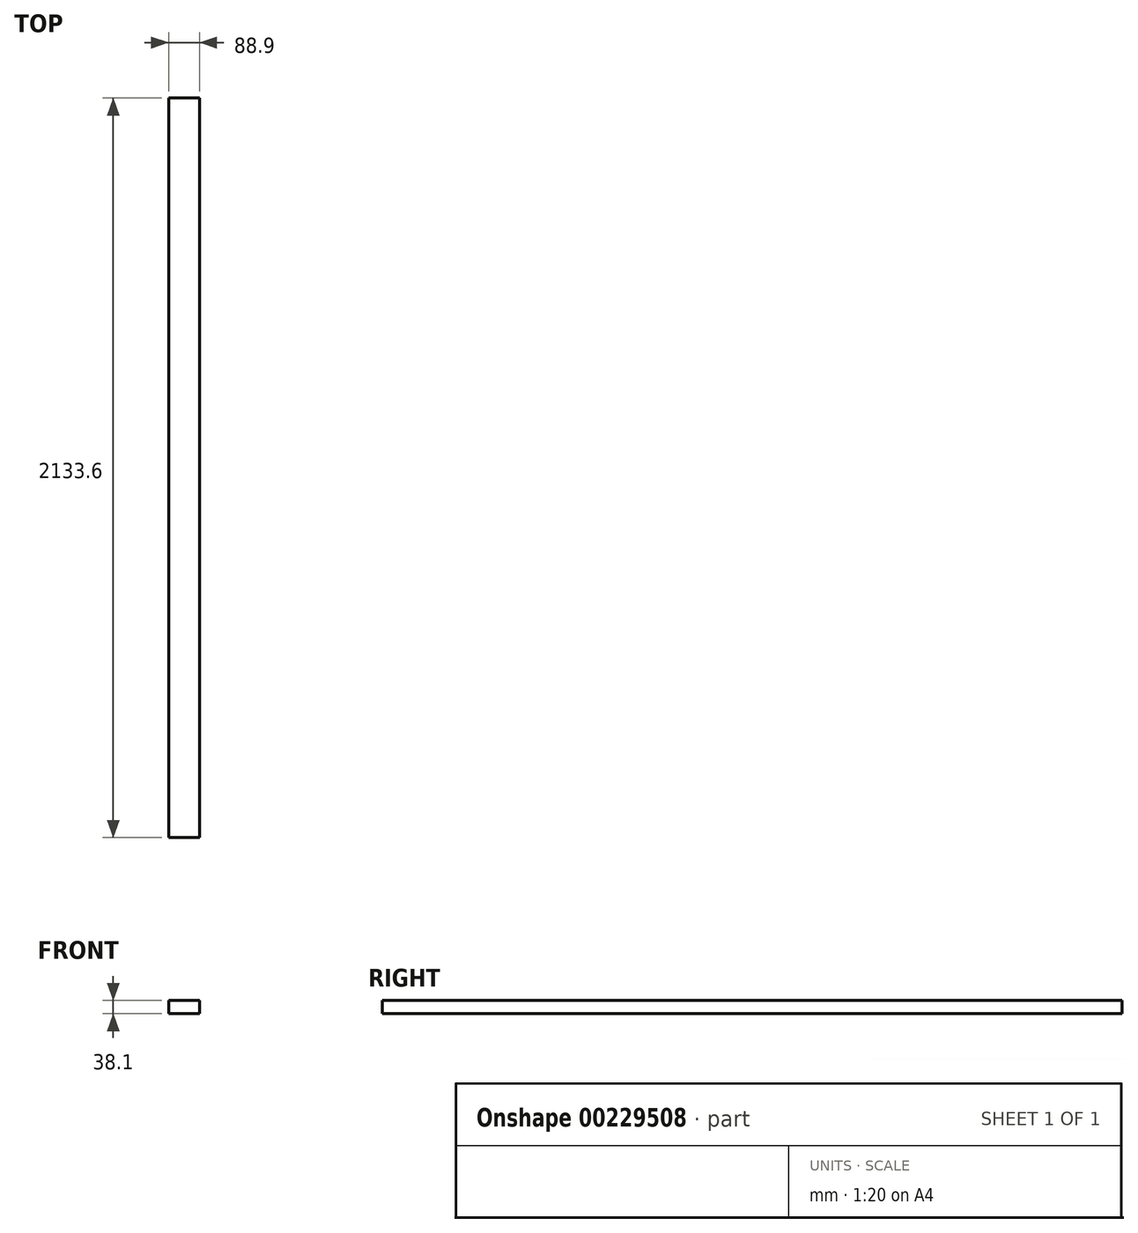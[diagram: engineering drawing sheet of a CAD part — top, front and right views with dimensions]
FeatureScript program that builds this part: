
annotation { "Feature Type Name" : "Feature", "Feature Type Description" : "" }
export const myFeature = defineFeature(function(context is Context, id is Id, definition is map)
    precondition{}
    {
        {
            var Q0;
            Q0=qCreatedBy(makeId("Front.planeOp"),FACE);
            var sketch = newSketch(context, id + "F0", { "sketchPlane" : qUnion([Q0])});
            skLineSegment(sketch, "E0.bottom", {"start": v(0, 0) * mm, "end": v(88.9, 0) * mm});
            skLineSegment(sketch, "E0.top", {"start": v(0, -38.1) * mm, "end": v(88.9, -38.1) * mm});
            skLineSegment(sketch, "E0.left", {"start": v(0, 0) * mm, "end": v(0, -38.1) * mm});
            skLineSegment(sketch, "E0.right", {"start": v(88.9, 0) * mm, "end": v(88.9, -38.1) * mm});
            skSolve(sketch);
        }
        {
            var Q0;
            Q0=qSketchRegion(id+"F0",true);
            extrude(context, id + "F1", {"entities" : qUnion([Q0]), "depth" : 2133.6 * mm});
        }
    });
